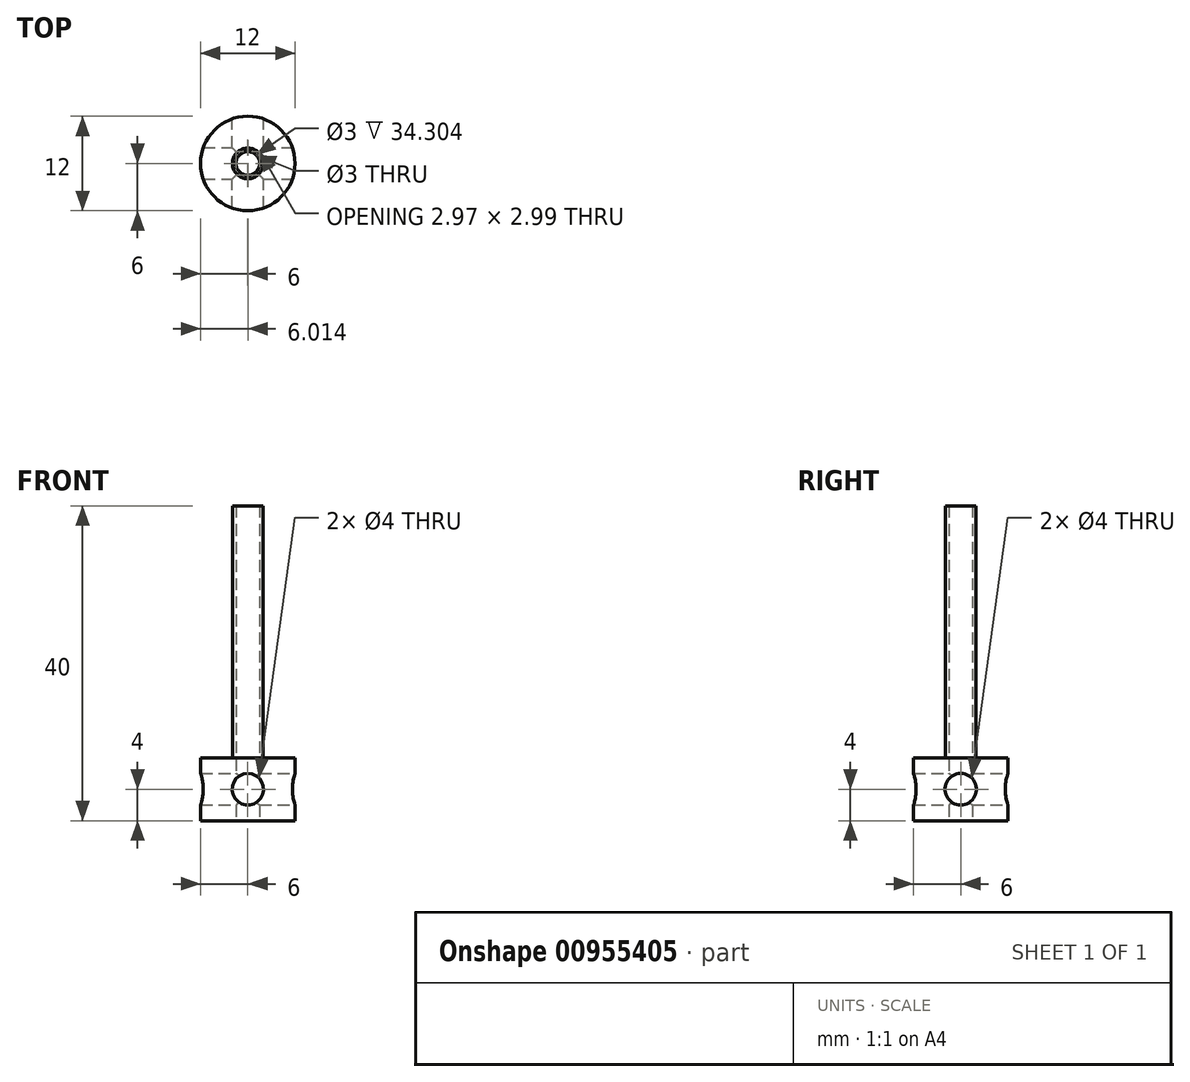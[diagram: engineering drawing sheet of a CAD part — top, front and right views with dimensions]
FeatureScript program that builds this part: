
annotation { "Feature Type Name" : "Feature", "Feature Type Description" : "" }
export const myFeature = defineFeature(function(context is Context, id is Id, definition is map)
    precondition{}
    {
        {
            var Q0;
            Q0=qCreatedBy(makeId("Top.planeOp"),FACE);
            var sketch = newSketch(context, id + "F0", { "sketchPlane" : qUnion([Q0])});
            skCircle(sketch, "E0", {"center": v(0, 0) * mm, "radius": 1.5 * mm});
            skCircle(sketch, "E1", {"center": v(0, 0) * mm, "radius": 1.95 * mm});
            skSolve(sketch);
        }
        {
            var Q0;
            Q0 = qSketchRegion(id + "F0", true);
            extrude(context, id + "F1", {"entities" : qUnion([Q0]), "depth" : 40 * mm, "offsetDistance" : 25 * mm});
        }
        {
            var Q0;
            Q0=qCreatedBy(makeId("Top.planeOp"),FACE);
            var sketch = newSketch(context, id + "F2", { "sketchPlane" : qUnion([Q0])});
            skCircle(sketch, "E2", {"center": v(0, 0) * mm, "radius": 1.5 * mm});
            skCircle(sketch, "E3", {"center": v(0, 0) * mm, "radius": 6 * mm});
            skSolve(sketch);
        }
        {
            var Q0;
            Q0 = qSketchRegion(id + "F2", true);
            extrude(context, id + "F3", {"entities" : qUnion([Q0]), "operationType" : NewBodyOperationType.ADD, "depth" : 8 * mm, "offsetDistance" : 25 * mm});
        }
        {
            var Q0;
            Q0=qCreatedBy(makeId("Front.planeOp"),FACE);
            var sketch = newSketch(context, id + "F4", { "sketchPlane" : qUnion([Q0])});
            skCircle(sketch, "E4", {"center": v(0, 4) * mm, "radius": 2 * mm});
            skSolve(sketch);
        }
        {
            var Q0;
            Q0 = qSketchRegion(id + "F4", true);
            extrude(context, id + "F5", {"entities" : qUnion([Q0]), "operationType" : NewBodyOperationType.REMOVE, "endBound" : BoundingType.SYMMETRIC, "depth" : 25 * mm, "offsetDistance" : 25 * mm});
        }
        {
            var Q0;
            Q0=qCreatedBy(makeId("Right.planeOp"),FACE);
            var sketch = newSketch(context, id + "F6", { "sketchPlane" : qUnion([Q0])});
            skCircle(sketch, "E5", {"center": v(0, 4) * mm, "radius": 2 * mm});
            skSolve(sketch);
        }
        {
            var Q0;
            Q0 = qSketchRegion(id + "F6", true);
            extrude(context, id + "F7", {"entities" : qUnion([Q0]), "operationType" : NewBodyOperationType.REMOVE, "endBound" : BoundingType.SYMMETRIC, "oppositeDirection" : true, "depth" : 25 * mm, "offsetDistance" : 25 * mm});
        }
    });
